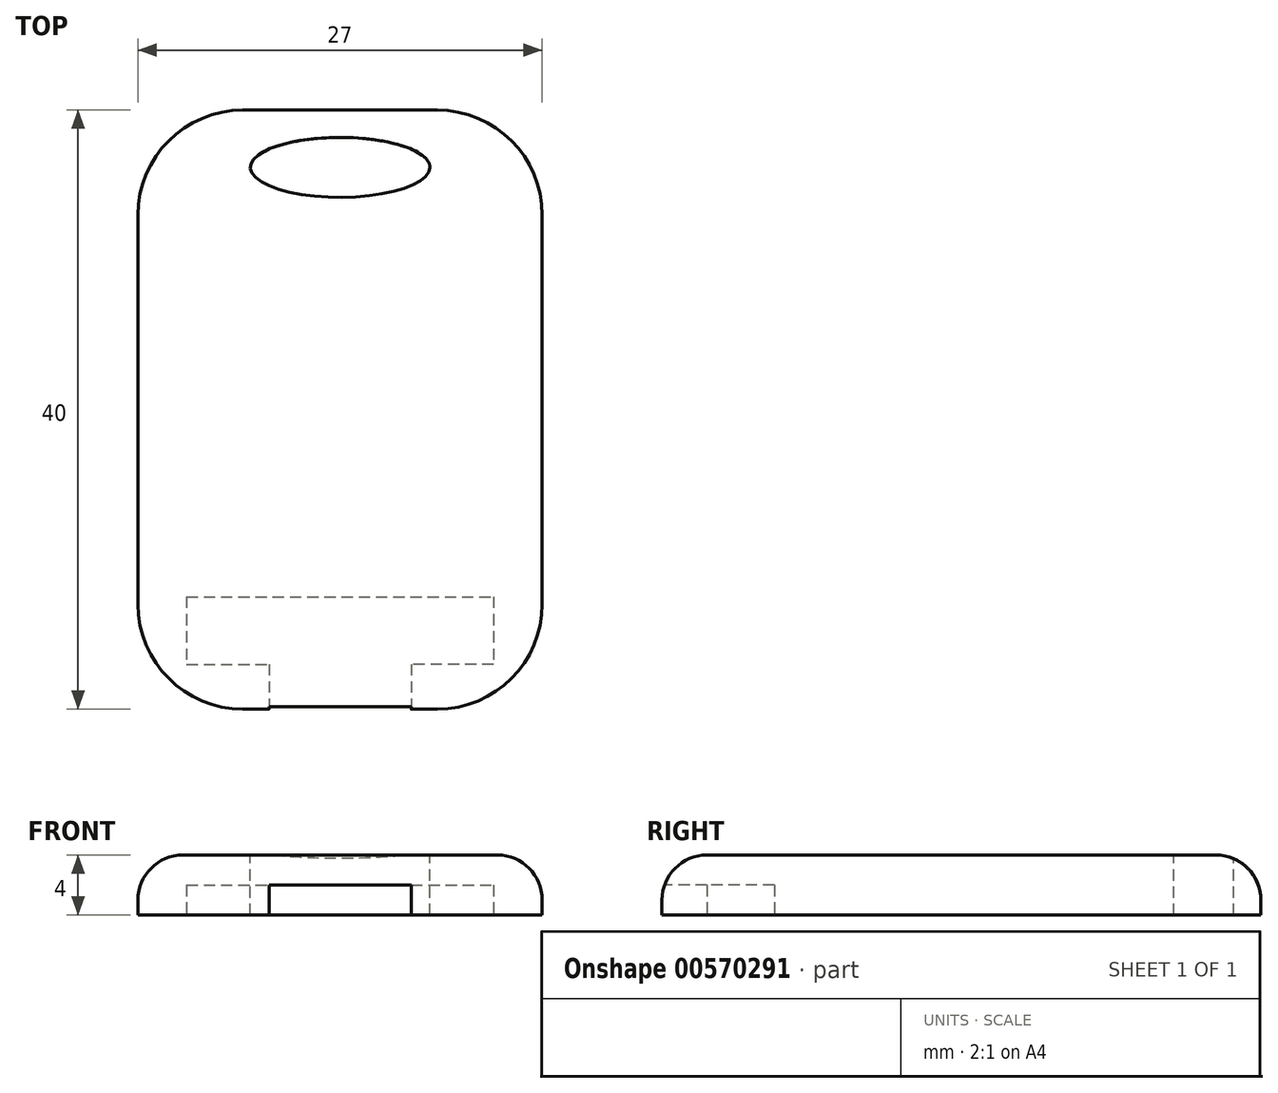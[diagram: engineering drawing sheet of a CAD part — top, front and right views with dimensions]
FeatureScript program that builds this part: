
annotation { "Feature Type Name" : "Feature", "Feature Type Description" : "" }
export const myFeature = defineFeature(function(context is Context, id is Id, definition is map)
    precondition{}
    {
        {
            var Q0;
            Q0=qCreatedBy(makeId("Top.planeOp"),FACE);
            var sketch = newSketch(context, id + "F0", { "sketchPlane" : qUnion([Q0])});
            skLineSegment(sketch, "E0", {"start": v(-7.45, 15.24) * mm, "end": v(13.05, 15.24) * mm});
            skLineSegment(sketch, "E1", {"start": v(13.05, 15.24) * mm, "end": v(13.05, 10.74) * mm});
            skLineSegment(sketch, "E2", {"start": v(13.05, 10.74) * mm, "end": v(7.55, 10.74) * mm});
            skLineSegment(sketch, "E3", {"start": v(-7.45, 15.24) * mm, "end": v(-7.45, 10.74) * mm});
            skLineSegment(sketch, "E4", {"start": v(-7.45, 10.74) * mm, "end": v(-1.95, 10.74) * mm});
            skLineSegment(sketch, "E5", {"start": v(7.55, 10.74) * mm, "end": v(7.55, 7.74) * mm});
            skLineSegment(sketch, "E6", {"start": v(-1.95, 10.74) * mm, "end": v(-1.95, 7.74) * mm});
            skLineSegment(sketch, "E7", {"start": v(-1.95, 7.74) * mm, "end": v(-9.95, 7.74) * mm});
            skLineSegment(sketch, "E8", {"start": v(-9.95, 7.74) * mm, "end": v(-9.95, 17.74) * mm});
            skLineSegment(sketch, "E9", {"start": v(-9.95, 17.74) * mm, "end": v(15.55, 17.74) * mm});
            skLineSegment(sketch, "E10", {"start": v(15.55, 17.74) * mm, "end": v(15.55, 7.74) * mm});
            skLineSegment(sketch, "E11", {"start": v(15.55, 7.74) * mm, "end": v(7.55, 7.74) * mm});
            skSolve(sketch);
        }
        {
            var Q0;
            Q0 = qSketchRegion(id + "F0", true);
            extrude(context, id + "F1", {"entities" : qUnion([Q0]), "depth" : 2 * mm, "offsetDistance" : 25 * mm});
        }
        {
            var Q0;
            Q0=makeQuery(id+"F1.opExtrude","CAP_FACE",FACE,{"disambiguationData":[OSD([sQuery(id+"F0.wireOp",EDGE,"E0"),sQuery(id+"F0.wireOp",EDGE,"E1"),sQuery(id+"F0.wireOp",EDGE,"E2"),sQuery(id+"F0.wireOp",EDGE,"E3"),sQuery(id+"F0.wireOp",EDGE,"E4"),sQuery(id+"F0.wireOp",EDGE,"E5"),sQuery(id+"F0.wireOp",EDGE,"E6"),sQuery(id+"F0.wireOp",EDGE,"E7"),sQuery(id+"F0.wireOp",EDGE,"E8"),sQuery(id+"F0.wireOp",EDGE,"E9"),sQuery(id+"F0.wireOp",EDGE,"E10"),sQuery(id+"F0.wireOp",EDGE,"E11")])],"isStart":false});
            var sketch = newSketch(context, id + "F2", { "sketchPlane" : qUnion([Q0])});
            skLineSegment(sketch, "E12.bottom", {"start": v(-9.95, 17.74) * mm, "end": v(15.55, 17.74) * mm});
            skLineSegment(sketch, "E12.top", {"start": v(-9.95, 7.74) * mm, "end": v(15.55, 7.74) * mm});
            skLineSegment(sketch, "E12.left", {"start": v(-9.95, 17.74) * mm, "end": v(-9.95, 7.74) * mm});
            skLineSegment(sketch, "E12.right", {"start": v(15.55, 17.74) * mm, "end": v(15.55, 7.74) * mm});
            skSolve(sketch);
        }
        {
            var Q0;
            Q0 = qSketchRegion(id + "F2", true);
            var Q1;
            Q1 = qSketchRegion(id + "F0", true);
            extrude(context, id + "F3", {"entities" : qUnion([Q0, Q1]), "operationType" : NewBodyOperationType.ADD, "depth" : 2 * mm, "offsetDistance" : 25 * mm});
        }
        {
            var Q0;
            Q0=makeQuery(id+"F3.boolean.opBoolean","MERGE",FACE,{"derivedFrom":[makeQuery(id+"F1.opExtrude","SWEPT_FACE",FACE,{"disambiguationData":[OSD([sQuery(id+"F0.wireOp",EDGE,"E8")])]}),makeQuery(id+"F3.opExtrude","SWEPT_FACE",FACE,{"disambiguationData":[OSD([sQuery(id+"F2.wireOp",EDGE,"E12.left")])]})]});
            extrude(context, id + "F4", {"entities" : qUnion([Q0]), "operationType" : NewBodyOperationType.ADD, "depth" : .75 * mm, "offsetDistance" : 25 * mm});
        }
        {
            var Q0;
            Q0=makeQuery(id+"F3.boolean.opBoolean","MERGE",FACE,{"derivedFrom":[makeQuery(id+"F1.opExtrude","SWEPT_FACE",FACE,{"disambiguationData":[OSD([sQuery(id+"F0.wireOp",EDGE,"E10")])]}),makeQuery(id+"F3.opExtrude","SWEPT_FACE",FACE,{"disambiguationData":[OSD([sQuery(id+"F2.wireOp",EDGE,"E12.right")])]})]});
            var Q1;
            Q1 = qSketchRegion(id + "FXTZOLMUWO4B4Ll_1", true);
            extrude(context, id + "F5", {"entities" : qUnion([Q0, Q1]), "operationType" : NewBodyOperationType.ADD, "depth" : .75 * mm, "offsetDistance" : 25 * mm});
        }
        {
            var Q0;
            {var subQ0=sQuery(id+"F2.wireOp",EDGE,"E12.bottom");var subQ1=sQuery(id+"F0.wireOp",EDGE,"E9");Q0=makeQuery(id+"F5.boolean.opBoolean","MERGE",FACE,{"derivedFrom":[makeQuery(id+"F4.boolean.opBoolean","MERGE",FACE,{"derivedFrom":[makeQuery(id+"F3.boolean.opBoolean","MERGE",FACE,{"derivedFrom":[makeQuery(id+"F1.opExtrude","SWEPT_FACE",FACE,{"disambiguationData":[OSD([subQ1])]}),makeQuery(id+"F3.opExtrude","SWEPT_FACE",FACE,{"disambiguationData":[OSD([subQ0])]})]}),makeQuery(id+"F4.opExtrude","SWEPT_FACE",FACE,{"disambiguationData":[OSD([sQuery(id+"F0.wireOp",EDGE,"E8"),subQ1,subQ0,sQuery(id+"F2.wireOp",EDGE,"E12.left")])]})]}),makeQuery(id+"F5.opExtrude","SWEPT_FACE",FACE,{"disambiguationData":[OSD([subQ1,sQuery(id+"F0.wireOp",EDGE,"E10"),subQ0,sQuery(id+"F2.wireOp",EDGE,"E12.right")])]})]});}
            extrude(context, id + "F6", {"entities" : qUnion([Q0]), "operationType" : NewBodyOperationType.ADD, "depth" : 30 * mm, "offsetDistance" : 25 * mm});
        }
        {
            var Q0;
            {var subQ0=sQuery(id+"F2.wireOp",EDGE,"E12.right");var subQ1=sQuery(id+"F2.wireOp",EDGE,"E12.left");var subQ2=sQuery(id+"F2.wireOp",EDGE,"E12.bottom");Q0=makeQuery(id+"F6.boolean.opBoolean","MERGE",FACE,{"derivedFrom":[makeQuery(id+"F5.boolean.opBoolean","MERGE",FACE,{"derivedFrom":[makeQuery(id+"F4.boolean.opBoolean","MERGE",FACE,{"derivedFrom":[makeQuery(id+"F3.opExtrude","CAP_FACE",FACE,{"disambiguationData":[OSD([subQ2,sQuery(id+"F2.wireOp",EDGE,"E12.top"),subQ1,subQ0])],"isStart":false}),makeQuery(id+"F4.opExtrude","SWEPT_FACE",FACE,{"disambiguationData":[OSD([subQ1])]})]}),makeQuery(id+"F5.opExtrude","SWEPT_FACE",FACE,{"disambiguationData":[OSD([subQ0])]})]}),makeQuery(id+"F6.opExtrude","SWEPT_FACE",FACE,{"disambiguationData":[OSD([subQ2,subQ1,subQ0])]})]});}
            var sketch = newSketch(context, id + "F7", { "sketchPlane" : qUnion([Q0])});
            skPoint(sketch, "E13", {"position": v(16.3, 47.74) * mm});
            skPoint(sketch, "E14", {"position": v(16.3, 7.74) * mm});
            skPoint(sketch, "E15", {"position": v(-10.7, 7.74) * mm});
            skPoint(sketch, "E16", {"position": v(2.8, 47.74) * mm});
            skEllipse(sketch, "E17", {"center": v(2.8, 43.9) * mm, "majorRadius": 6 * mm, "minorRadius": 2 * mm, "majorAxis": v(1, 0)});
            skSolve(sketch);
        }
        {
            var Q0;
            {var subQ0=sQuery(id+"F2.wireOp",EDGE,"E12.right");Q0=makeQuery(id+"F6.boolean.opBoolean","MERGE",EDGE,{"derivedFrom":[makeQuery(id+"F5.opExtrude","CAP_EDGE",EDGE,{"disambiguationData":[OSD([subQ0])],"isStart":false}),makeQuery(id+"F6.opExtrude","SWEPT_EDGE",EDGE,{"disambiguationData":[OSD([sQuery(id+"F2.wireOp",EDGE,"E12.bottom"),subQ0])]})]});}
            var Q1;
            Q1=makeQuery(id+"F6.opExtrude","CAP_EDGE",EDGE,{"disambiguationData":[OSD([sQuery(id+"F2.wireOp",EDGE,"E12.bottom"),sQuery(id+"F2.wireOp",EDGE,"E12.left"),sQuery(id+"F2.wireOp",EDGE,"E12.right")])],"isStart":false});
            var Q2;
            {var subQ0=sQuery(id+"F2.wireOp",EDGE,"E12.left");Q2=makeQuery(id+"F6.boolean.opBoolean","MERGE",EDGE,{"derivedFrom":[makeQuery(id+"F4.opExtrude","CAP_EDGE",EDGE,{"disambiguationData":[OSD([subQ0])],"isStart":false}),makeQuery(id+"F6.opExtrude","SWEPT_EDGE",EDGE,{"disambiguationData":[OSD([sQuery(id+"F2.wireOp",EDGE,"E12.bottom"),subQ0])]})]});}
            var Q3;
            {var subQ0=sQuery(id+"F2.wireOp",EDGE,"E12.top");Q3=makeQuery(id+"F5.boolean.opBoolean","MERGE",EDGE,{"derivedFrom":[makeQuery(id+"F4.boolean.opBoolean","MERGE",EDGE,{"derivedFrom":[makeQuery(id+"F3.opExtrude","CAP_EDGE",EDGE,{"disambiguationData":[OSD([subQ0])],"isStart":false}),makeQuery(id+"F4.opExtrude","SWEPT_EDGE",EDGE,{"disambiguationData":[OSD([subQ0,sQuery(id+"F2.wireOp",EDGE,"E12.left")])]})]}),makeQuery(id+"F5.opExtrude","SWEPT_EDGE",EDGE,{"disambiguationData":[OSD([subQ0,sQuery(id+"F2.wireOp",EDGE,"E12.right")])]})]});}
            fillet(context, id + "F8", {"entities" : qUnion([Q0, Q1, Q2, Q3]), "radius" : 3 * mm, "tangentPropagation" : true, "allowEdgeOverflow" : false});
        }
        {
            var Q0;
            Q0 = qSketchRegion(id + "F7", true);
            extrude(context, id + "F9", {"entities" : qUnion([Q0]), "operationType" : NewBodyOperationType.REMOVE, "oppositeDirection" : true, "depth" : 25 * mm, "offsetDistance" : 25 * mm});
        }
        {
            var Q0;
            {var subQ0=sQuery(id+"F2.wireOp",EDGE,"E12.right");var subQ1=sQuery(id+"F2.wireOp",EDGE,"E12.top");Q0=makeQuery(id+"F8.opFillet","BLEND_EDGE",EDGE,{"blendedFrom":[makeQuery(id+"F5.boolean.opBoolean","MERGE",EDGE,{"derivedFrom":[makeQuery(id+"F4.boolean.opBoolean","MERGE",EDGE,{"derivedFrom":[makeQuery(id+"F3.opExtrude","CAP_EDGE",EDGE,{"disambiguationData":[OSD([subQ1])],"isStart":false}),makeQuery(id+"F4.opExtrude","SWEPT_EDGE",EDGE,{"disambiguationData":[OSD([subQ1,sQuery(id+"F2.wireOp",EDGE,"E12.left")])]})]}),makeQuery(id+"F5.opExtrude","SWEPT_EDGE",EDGE,{"disambiguationData":[OSD([subQ1,subQ0])]})]}),makeQuery(id+"F6.boolean.opBoolean","MERGE",EDGE,{"derivedFrom":[makeQuery(id+"F5.opExtrude","CAP_EDGE",EDGE,{"disambiguationData":[OSD([subQ0])],"isStart":false}),makeQuery(id+"F6.opExtrude","SWEPT_EDGE",EDGE,{"disambiguationData":[OSD([sQuery(id+"F2.wireOp",EDGE,"E12.bottom"),subQ0])]})]})],"blendedInto":[]});}
            var Q1;
            {var subQ0=sQuery(id+"F2.wireOp",EDGE,"E12.left");var subQ1=sQuery(id+"F2.wireOp",EDGE,"E12.top");Q1=makeQuery(id+"F8.opFillet","BLEND_EDGE",EDGE,{"blendedFrom":[makeQuery(id+"F5.boolean.opBoolean","MERGE",EDGE,{"derivedFrom":[makeQuery(id+"F4.boolean.opBoolean","MERGE",EDGE,{"derivedFrom":[makeQuery(id+"F3.opExtrude","CAP_EDGE",EDGE,{"disambiguationData":[OSD([subQ1])],"isStart":false}),makeQuery(id+"F4.opExtrude","SWEPT_EDGE",EDGE,{"disambiguationData":[OSD([subQ1,subQ0])]})]}),makeQuery(id+"F5.opExtrude","SWEPT_EDGE",EDGE,{"disambiguationData":[OSD([subQ1,sQuery(id+"F2.wireOp",EDGE,"E12.right")])]})]}),makeQuery(id+"F6.boolean.opBoolean","MERGE",EDGE,{"derivedFrom":[makeQuery(id+"F4.opExtrude","CAP_EDGE",EDGE,{"disambiguationData":[OSD([subQ0])],"isStart":false}),makeQuery(id+"F6.opExtrude","SWEPT_EDGE",EDGE,{"disambiguationData":[OSD([sQuery(id+"F2.wireOp",EDGE,"E12.bottom"),subQ0])]})]})],"blendedInto":[]});}
            var Q2;
            {var subQ0=sQuery(id+"F2.wireOp",EDGE,"E12.left");var subQ1=sQuery(id+"F2.wireOp",EDGE,"E12.bottom");Q2=makeQuery(id+"F8.opFillet","BLEND_EDGE",EDGE,{"blendedFrom":[makeQuery(id+"F6.opExtrude","CAP_EDGE",EDGE,{"disambiguationData":[OSD([subQ1,subQ0,sQuery(id+"F2.wireOp",EDGE,"E12.right")])],"isStart":false}),makeQuery(id+"F6.boolean.opBoolean","MERGE",EDGE,{"derivedFrom":[makeQuery(id+"F4.opExtrude","CAP_EDGE",EDGE,{"disambiguationData":[OSD([subQ0])],"isStart":false}),makeQuery(id+"F6.opExtrude","SWEPT_EDGE",EDGE,{"disambiguationData":[OSD([subQ1,subQ0])]})]})],"blendedInto":[]});}
            var Q3;
            {var subQ0=sQuery(id+"F2.wireOp",EDGE,"E12.right");var subQ1=sQuery(id+"F2.wireOp",EDGE,"E12.bottom");Q3=makeQuery(id+"F8.opFillet","BLEND_EDGE",EDGE,{"blendedFrom":[makeQuery(id+"F6.opExtrude","CAP_EDGE",EDGE,{"disambiguationData":[OSD([subQ1,sQuery(id+"F2.wireOp",EDGE,"E12.left"),subQ0])],"isStart":false}),makeQuery(id+"F6.boolean.opBoolean","MERGE",EDGE,{"derivedFrom":[makeQuery(id+"F5.opExtrude","CAP_EDGE",EDGE,{"disambiguationData":[OSD([subQ0])],"isStart":false}),makeQuery(id+"F6.opExtrude","SWEPT_EDGE",EDGE,{"disambiguationData":[OSD([subQ1,subQ0])]})]})],"blendedInto":[]});}
            fillet(context, id + "F10", {"entities" : qUnion([Q0, Q1, Q2, Q3]), "radius" : 7 * mm, "tangentPropagation" : true, "allowEdgeOverflow" : false});
        }
    });
